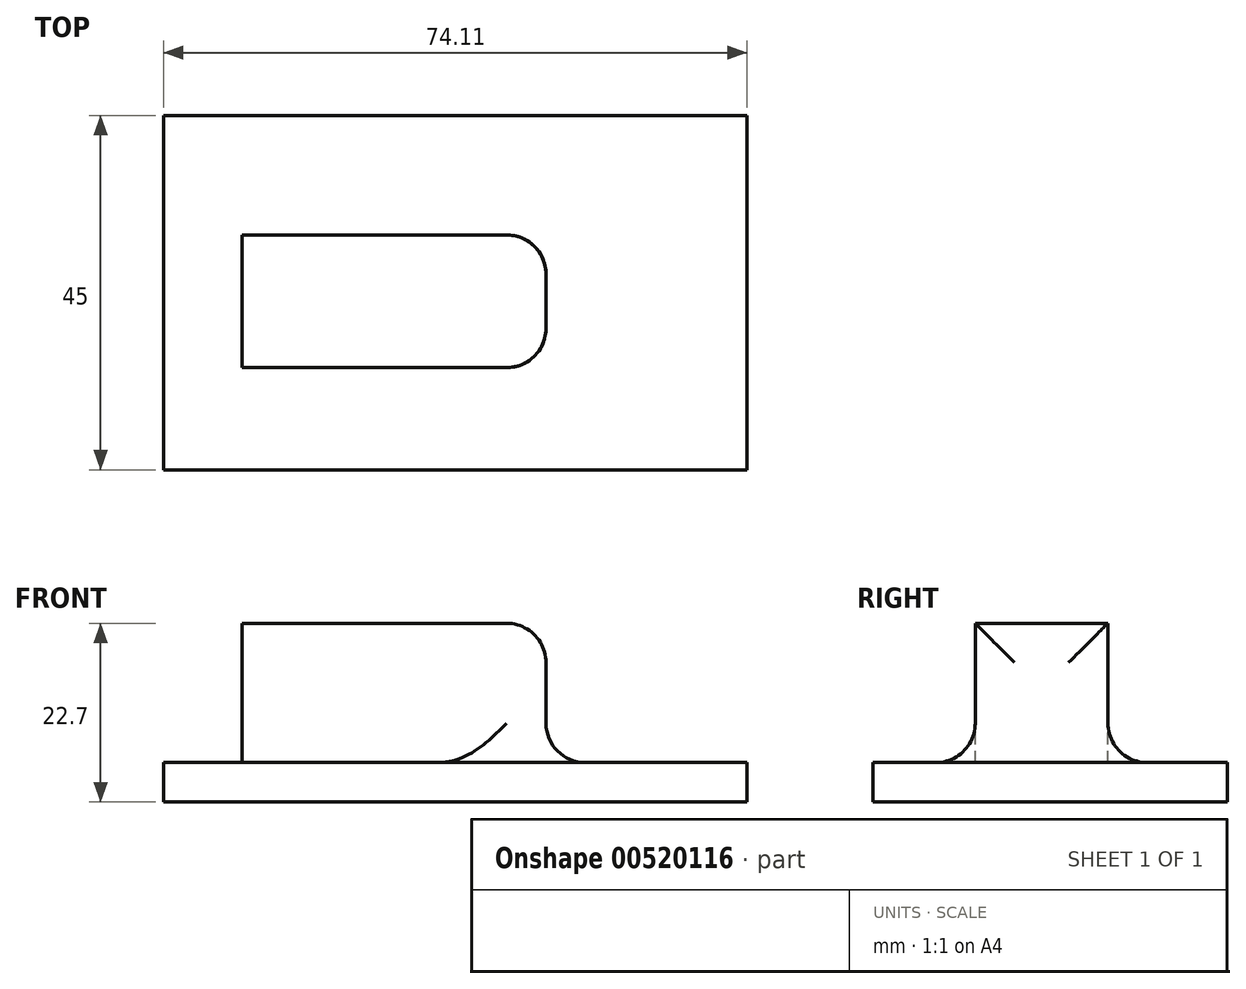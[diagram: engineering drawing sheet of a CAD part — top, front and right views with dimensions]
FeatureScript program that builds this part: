
annotation { "Feature Type Name" : "Feature", "Feature Type Description" : "" }
export const myFeature = defineFeature(function(context is Context, id is Id, definition is map)
    precondition{}
    {
        {
            var Q0;
            Q0=qCreatedBy(makeId("Top.planeOp"),FACE);
            var sketch = newSketch(context, id + "F0", { "sketchPlane" : qUnion([Q0])});
            skLineSegment(sketch, "E0.bottom", {"start": v(0, 0) * mm, "end": v(74.11, 0) * mm});
            skLineSegment(sketch, "E0.top", {"start": v(0, 45) * mm, "end": v(74.11, 45) * mm});
            skLineSegment(sketch, "E0.left", {"start": v(0, 0) * mm, "end": v(0, 45) * mm});
            skLineSegment(sketch, "E0.right", {"start": v(74.11, 0) * mm, "end": v(74.11, 45) * mm});
            skSolve(sketch);
        }
        {
            var Q0;
            Q0 = qSketchRegion(id + "F0", true);
            extrude(context, id + "F1", {"entities" : qUnion([Q0]), "depth" : 5 * mm, "offsetDistance" : 25 * mm});
        }
        {
            var Q0;
            Q0=makeQuery(id+"F1.opExtrude","CAP_FACE",FACE,{"disambiguationData":[OSD([sQuery(id+"F0.wireOp",EDGE,"E0.bottom"),sQuery(id+"F0.wireOp",EDGE,"E0.top"),sQuery(id+"F0.wireOp",EDGE,"E0.left"),sQuery(id+"F0.wireOp",EDGE,"E0.right")])],"isStart":false});
            var sketch = newSketch(context, id + "F2", { "sketchPlane" : qUnion([Q0])});
            skSolve(sketch);
        }
        {
            var Q0;
            Q0=makeQuery(id+"F2.imprint","IMPRINT",FACE,{"disambiguationData":[TD([[makeQuery(id+"F2.imprint","IMPRINT",EDGE,{"derivedFrom":makeQuery(id+"F1.opExtrude","CAP_EDGE",EDGE,{"disambiguationData":[OSD([sQuery(id+"F0.wireOp",EDGE,"E0.bottom")])],"isStart":false})}),1.0]])]});
            var sketch = newSketch(context, id + "F3", { "sketchPlane" : qUnion([Q0])});
            skLineSegment(sketch, "E1.bottom", {"start": v(48.57, 12.98) * mm, "end": v(9.94, 12.98) * mm});
            skLineSegment(sketch, "E1.top", {"start": v(48.57, 29.84) * mm, "end": v(9.94, 29.84) * mm});
            skLineSegment(sketch, "E1.left", {"start": v(48.57, 12.98) * mm, "end": v(48.57, 29.84) * mm});
            skLineSegment(sketch, "E1.right", {"start": v(9.94, 12.98) * mm, "end": v(9.94, 29.84) * mm});
            skSolve(sketch);
        }
        {
            var Q0;
            Q0=makeQuery(id+"F3.imprint","IMPRINT",FACE,{"disambiguationData":[TD([[makeQuery(id+"F3.imprint","IMPRINT",EDGE,{"derivedFrom":sQuery(id+"F3.wireOp",EDGE,"E1.bottom")}),-1.0]])]});
            extrude(context, id + "F4", {"entities" : qUnion([Q0]), "operationType" : NewBodyOperationType.ADD, "depth" : 17.7 * mm, "offsetDistance" : 25 * mm});
        }
        {
            var Q0;
            Q0=makeQuery(id+"F4.opExtrude","SWEPT_FACE",FACE,{"disambiguationData":[OSD([sQuery(id+"F3.wireOp",EDGE,"E1.left")])]});
            fillet(context, id + "F5", {"entities" : qUnion([Q0]), "radius" : 5 * mm, "tangentPropagation" : true, "allowEdgeOverflow" : false});
        }
    });
